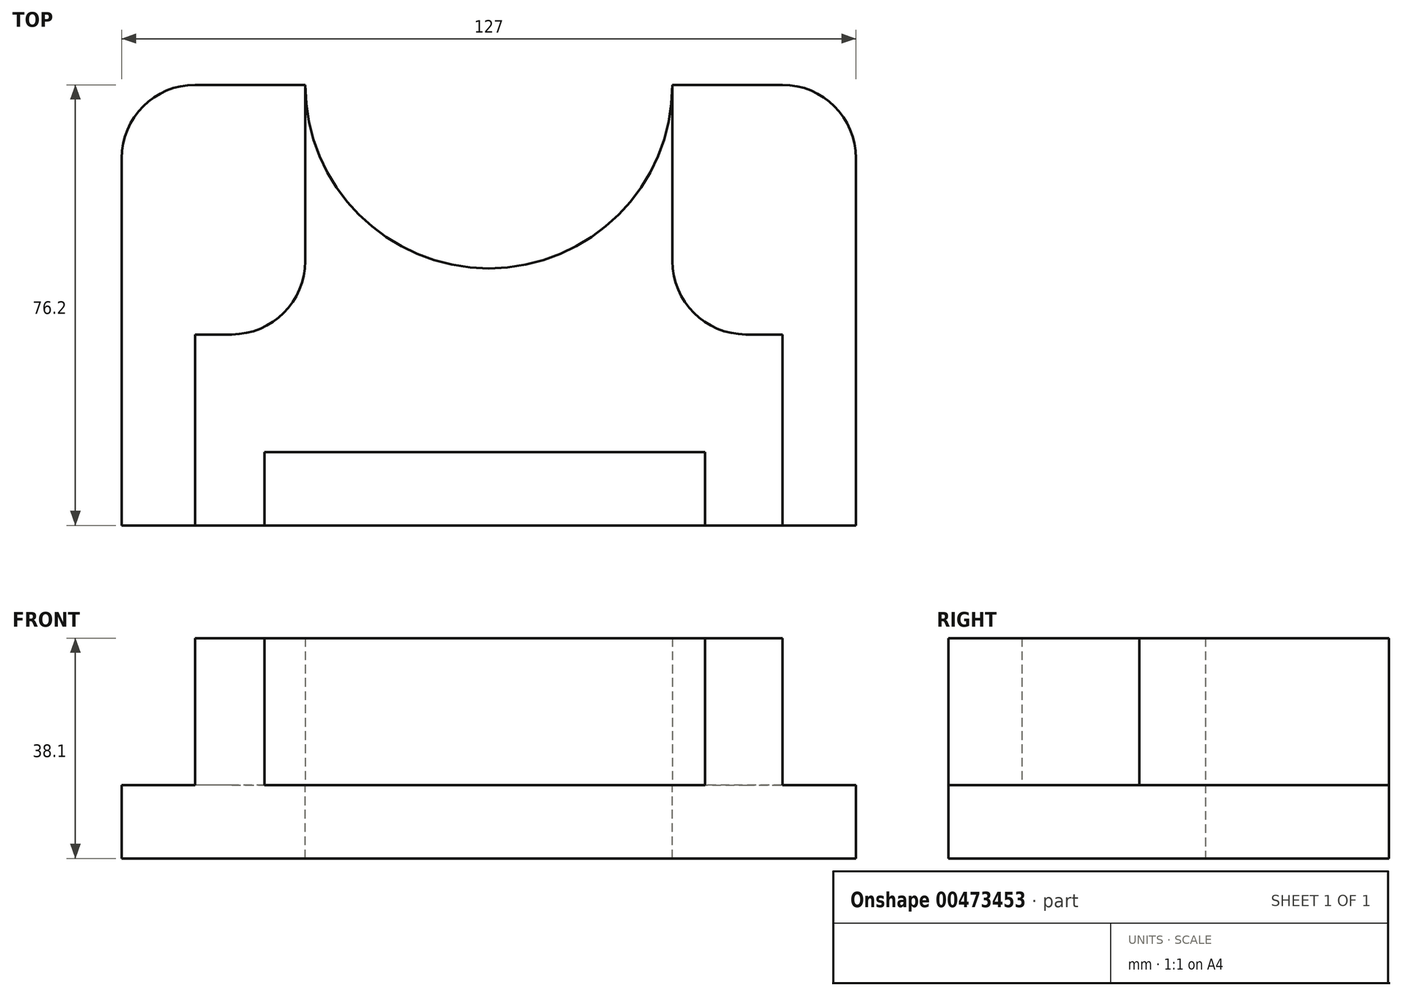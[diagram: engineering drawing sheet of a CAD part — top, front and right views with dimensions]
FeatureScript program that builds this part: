
annotation { "Feature Type Name" : "Feature", "Feature Type Description" : "" }
export const myFeature = defineFeature(function(context is Context, id is Id, definition is map)
    precondition{}
    {
        {
            var Q0;
            Q0=qCreatedBy(makeId("Top.planeOp"),FACE);
            var sketch = newSketch(context, id + "F0", { "sketchPlane" : qUnion([Q0])});
            skLineSegment(sketch, "E0.bottom", {"start": v(63.5, 38.1) * mm, "end": v(-63.5, 38.1) * mm});
            skLineSegment(sketch, "E0.top", {"start": v(63.5, -38.1) * mm, "end": v(-63.5, -38.1) * mm});
            skLineSegment(sketch, "E0.left", {"start": v(63.5, 38.1) * mm, "end": v(63.5, -38.1) * mm});
            skLineSegment(sketch, "E0.right", {"start": v(-63.5, 38.1) * mm, "end": v(-63.5, -38.1) * mm});
            skPoint(sketch, "E0.middle", {"position": v(0, 0) * mm});
            skSolve(sketch);
        }
        {
            var Q0;
            Q0=makeQuery(id+"F0.imprint","IMPRINT",FACE,{"disambiguationData":[TD([[makeQuery(id+"F0.imprint","IMPRINT",EDGE,{"derivedFrom":sQuery(id+"F0.wireOp",EDGE,"E0.bottom")}),1.0]])]});
            extrude(context, id + "F1", {"entities" : qUnion([Q0]), "depth" : 12.7 * mm});
        }
        {
            var Q0;
            Q0=makeQuery(id+"F1.opExtrude","CAP_FACE",FACE,{"disambiguationData":[OSD([sQuery(id+"F0.wireOp",EDGE,"E0.bottom"),sQuery(id+"F0.wireOp",EDGE,"E0.top"),sQuery(id+"F0.wireOp",EDGE,"E0.left"),sQuery(id+"F0.wireOp",EDGE,"E0.right")])],"isStart":false});
            var sketch = newSketch(context, id + "F2", { "sketchPlane" : qUnion([Q0])});
            skCircle(sketch, "E1", {"center": v(0, 38.1) * mm, "radius": 31.75 * mm});
            skLineSegment(sketch, "E2", {"start": v(-31.75, 38.1) * mm, "end": v(-31.75, 7.62) * mm});
            skLineSegment(sketch, "E3", {"start": v(-44.45, -5.08) * mm, "end": v(-50.8, -5.08) * mm});
            skLineSegment(sketch, "E4", {"start": v(-50.8, -5.08) * mm, "end": v(-50.8, -38.1) * mm});
            skLineSegment(sketch, "E5", {"start": v(-50.8, -38.1) * mm, "end": v(-38.8, -38.1) * mm});
            skLineSegment(sketch, "E6", {"start": v(-38.8, -38.1) * mm, "end": v(-38.8, -25.4) * mm});
            skLineSegment(sketch, "E7", {"start": v(-38.8, -25.4) * mm, "end": v(37.4, -25.4) * mm});
            skLineSegment(sketch, "E8", {"start": v(37.4, -25.4) * mm, "end": v(37.4, -38.1) * mm});
            skLineSegment(sketch, "E9", {"start": v(37.4, -38.1) * mm, "end": v(50.8, -38.1) * mm});
            skLineSegment(sketch, "E10", {"start": v(31.75, 38.1) * mm, "end": v(31.75, 7.62) * mm});
            skLineSegment(sketch, "E11", {"start": v(44.45, -5.08) * mm, "end": v(50.8, -5.08) * mm});
            skLineSegment(sketch, "E12", {"start": v(50.8, -5.08) * mm, "end": v(50.8, -38.1) * mm});
            skPoint(sketch, "E13.visualSharp", {"position": v(-31.75, -5.08) * mm});
            skArc(sketch, "E13.filletArc", {"start": v(-44.45, -5.08) * mm, "mid": v(-35.47, -1.36) * mm, "end": v(-31.75, 7.62) * mm});
            skPoint(sketch, "E14.visualSharp", {"position": v(31.75, -5.08) * mm});
            skArc(sketch, "E14.filletArc", {"start": v(31.75, 7.62) * mm, "mid": v(35.47, -1.36) * mm, "end": v(44.45, -5.08) * mm});
            skSolve(sketch);
        }
        {
            var Q0;
            {var subQ1=sQuery(id+"F2.wireOp",EDGE,"E2");Q0=makeQuery(id+"F2.imprint","IMPRINT",FACE,{"disambiguationData":[TD([[makeQuery(id+"F2.imprint","IMPRINT",EDGE,{"derivedFrom":subQ1}),1.0]])]});}
            extrude(context, id + "F3", {"entities" : qUnion([Q0]), "operationType" : NewBodyOperationType.ADD, "depth" : 25.4 * mm});
        }
        {
            var Q0;
            Q0=makeQuery(id+"F1.opExtrude","SWEPT_EDGE",EDGE,{"disambiguationData":[OSD([sQuery(id+"F0.wireOp",EDGE,"E0.bottom"),sQuery(id+"F0.wireOp",EDGE,"E0.right")])]});
            var Q1;
            Q1=makeQuery(id+"F1.opExtrude","SWEPT_EDGE",EDGE,{"disambiguationData":[OSD([sQuery(id+"F0.wireOp",EDGE,"E0.bottom"),sQuery(id+"F0.wireOp",EDGE,"E0.left")])]});
            fillet(context, id + "F4", {"entities" : qUnion([Q0, Q1]), "radius" : 12.7 * mm, "tangentPropagation" : true, "allowEdgeOverflow" : false});
        }
        {
            var Q0;
            {var subQ0=sQuery(id+"F0.wireOp",EDGE,"E0.bottom");var subQ1=makeQuery(id+"F1.opExtrude","CAP_FACE",FACE,{"disambiguationData":[OSD([subQ0,sQuery(id+"F0.wireOp",EDGE,"E0.top"),sQuery(id+"F0.wireOp",EDGE,"E0.left"),sQuery(id+"F0.wireOp",EDGE,"E0.right")])],"isStart":false});Q0=makeQuery(id+"F3.boolean.opBoolean","SPLIT",FACE,{"disambiguationData":[TD([makeQuery(id+"F1.opExtrude","SWEPT_FACE",FACE,{"disambiguationData":[OSD([subQ0])]}),subQ1,makeQuery(id+"F3.opExtrude","SWEPT_FACE",FACE,{"disambiguationData":[OSD([sQuery(id+"F2.wireOp",EDGE,"E1")])]}),makeQuery(id+"F3.opExtrude","SWEPT_FACE",FACE,{"disambiguationData":[OSD([sQuery(id+"F2.wireOp",EDGE,"E2")])]}),makeQuery(id+"F3.opExtrude","SWEPT_FACE",FACE,{"disambiguationData":[OSD([sQuery(id+"F2.wireOp",EDGE,"E10")])]})])],"derivedFrom":subQ1});}
            extrude(context, id + "F5", {"entities" : qUnion([Q0]), "operationType" : NewBodyOperationType.REMOVE, "endBound" : BoundingType.THROUGH_ALL, "oppositeDirection" : true, "depth" : 25.4 * mm});
        }
    });
